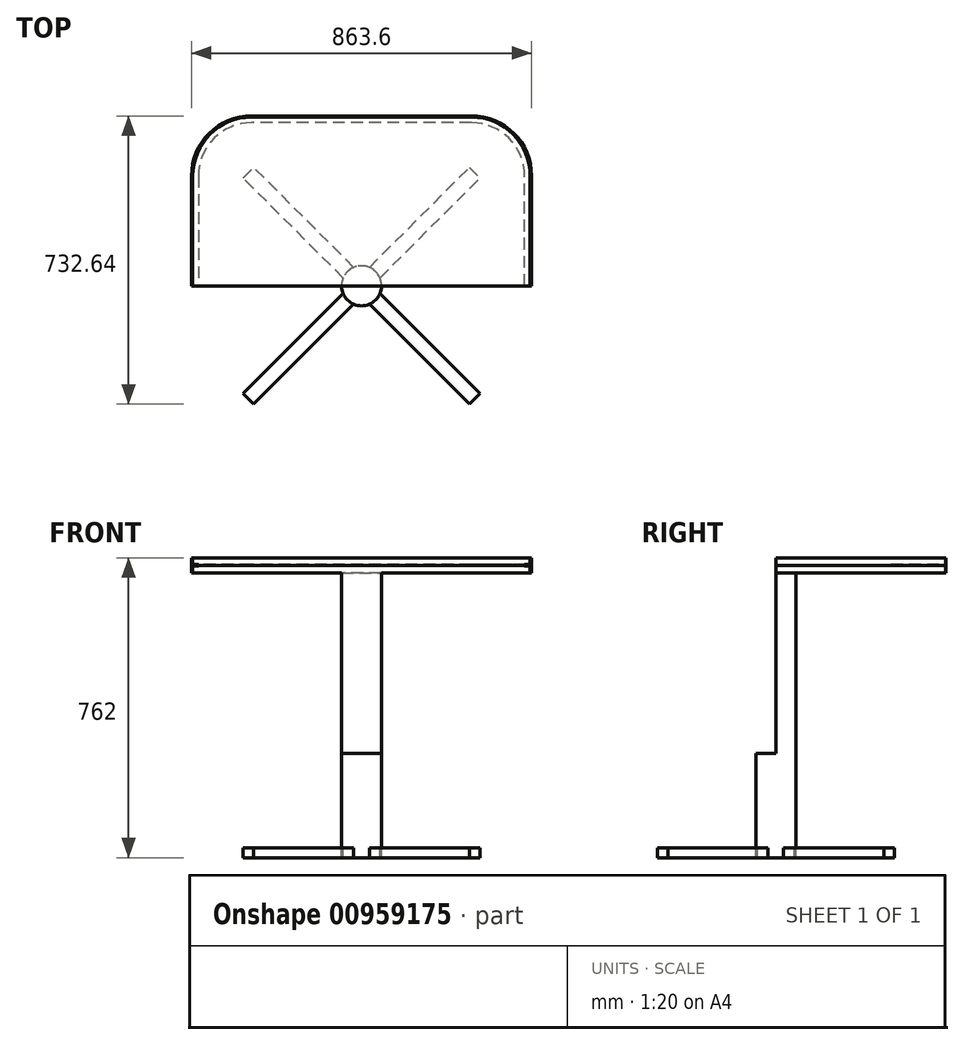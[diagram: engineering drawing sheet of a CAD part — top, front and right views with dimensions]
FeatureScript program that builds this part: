
annotation { "Feature Type Name" : "Feature", "Feature Type Description" : "" }
export const myFeature = defineFeature(function(context is Context, id is Id, definition is map)
    precondition{}
    {
        {
            var Q0;
            Q0=qCreatedBy(makeId("Top.planeOp"),FACE);
            var sketch = newSketch(context, id + "F0", { "sketchPlane" : qUnion([Q0])});
            skLineSegment(sketch, "E0.bottom", {"start": v(-279.4, 431.8) * mm, "end": v(279.4, 431.8) * mm});
            skLineSegment(sketch, "E0.top", {"start": v(-279.4, -431.8) * mm, "end": v(279.4, -431.8) * mm});
            skLineSegment(sketch, "E0.left", {"start": v(-431.8, 279.4) * mm, "end": v(-431.8, -279.4) * mm});
            skLineSegment(sketch, "E0.right", {"start": v(431.8, 279.4) * mm, "end": v(431.8, -279.4) * mm});
            skPoint(sketch, "E0.middle", {"position": v(0, 0) * mm});
            skPoint(sketch, "E1.visualSharp", {"position": v(-431.8, 431.8) * mm});
            skArc(sketch, "E1.filletArc", {"start": v(-279.4, 431.8) * mm, "mid": v(-387.16, 387.16) * mm, "end": v(-431.8, 279.4) * mm});
            skPoint(sketch, "E2.visualSharp", {"position": v(431.8, 431.8) * mm});
            skArc(sketch, "E2.filletArc", {"start": v(431.8, 279.4) * mm, "mid": v(387.16, 387.16) * mm, "end": v(279.4, 431.8) * mm});
            skPoint(sketch, "E3.visualSharp", {"position": v(431.8, -431.8) * mm});
            skArc(sketch, "E3.filletArc", {"start": v(279.4, -431.8) * mm, "mid": v(387.16, -387.16) * mm, "end": v(431.8, -279.4) * mm});
            skPoint(sketch, "E4.visualSharp", {"position": v(-431.8, -431.8) * mm});
            skArc(sketch, "E4.filletArc", {"start": v(-431.8, -279.4) * mm, "mid": v(-387.16, -387.16) * mm, "end": v(-279.4, -431.8) * mm});
            skSolve(sketch);
        }
        {
            var Q0;
            Q0=qSketchRegion(id+"F0",true);
            extrude(context, id + "F1", {"entities" : qUnion([Q0]), "oppositeDirection" : true, "depth" : 19.05 * mm, "offsetDistance" : 25.4 * mm});
        }
        {
            var Q0;
            Q0=makeQuery(id+"F1.opExtrude","CAP_FACE",FACE,{"disambiguationData":[OSD([sQuery(id+"F0.wireOp",EDGE,"E0.bottom"),sQuery(id+"F0.wireOp",EDGE,"E0.top"),sQuery(id+"F0.wireOp",EDGE,"E0.left"),sQuery(id+"F0.wireOp",EDGE,"E0.right"),sQuery(id+"F0.wireOp",EDGE,"E1.filletArc"),sQuery(id+"F0.wireOp",EDGE,"E2.filletArc"),sQuery(id+"F0.wireOp",EDGE,"E3.filletArc"),sQuery(id+"F0.wireOp",EDGE,"E4.filletArc")])],"isStart":false});
            var sketch = newSketch(context, id + "F2", { "sketchPlane" : qUnion([Q0])});
            skArc(sketch, "E5.0", {"start": v(-431.8, 279.4) * mm, "mid": v(-387.16, 387.16) * mm, "end": v(-279.4, 431.8) * mm});
            skLineSegment(sketch, "E6.0", {"start": v(-279.4, 431.8) * mm, "end": v(279.4, 431.8) * mm});
            skArc(sketch, "E7.0", {"start": v(279.4, 431.8) * mm, "mid": v(387.16, 387.16) * mm, "end": v(431.8, 279.4) * mm});
            skLineSegment(sketch, "E8.0", {"start": v(431.8, -279.4) * mm, "end": v(431.8, 279.4) * mm});
            skArc(sketch, "E9.0", {"start": v(431.8, -279.4) * mm, "mid": v(387.16, -387.16) * mm, "end": v(279.4, -431.8) * mm});
            skLineSegment(sketch, "E10.0", {"start": v(-279.4, -431.8) * mm, "end": v(279.4, -431.8) * mm});
            skArc(sketch, "E11.0", {"start": v(-279.4, -431.8) * mm, "mid": v(-387.16, -387.16) * mm, "end": v(-431.8, -279.4) * mm});
            skLineSegment(sketch, "E12.0", {"start": v(-431.8, -279.4) * mm, "end": v(-431.8, 279.4) * mm});
            skSolve(sketch);
        }
        {
            var Q0;
            Q0=makeQuery(id+"F2.imprint","IMPRINT",FACE,{"disambiguationData":[TD([[makeQuery(id+"F2.imprint","IMPRINT",EDGE,{"derivedFrom":sQuery(id+"F2.wireOp",EDGE,"E5.0")}),-1.0]])]});
            extrude(context, id + "F3", {"entities" : qUnion([Q0]), "depth" : 19.05 * mm, "offsetDistance" : 25.4 * mm});
        }
        {
            var Q0;
            Q0=qCreatedBy(makeId("Front.planeOp"),FACE);
            var sketch = newSketch(context, id + "F4", { "sketchPlane" : qUnion([Q0])});
            skLineSegment(sketch, "E13.0", {"start": v(-428.63, 0) * mm, "end": v(-431.8, 0) * mm});
            skLineSegment(sketch, "E14.0", {"start": v(-431.8, -19.05) * mm, "end": v(-431.8, 0) * mm});
            skLineSegment(sketch, "E15.0", {"start": v(-431.8, -38.1) * mm, "end": v(-431.8, -19.05) * mm});
            skLineSegment(sketch, "E16.0", {"start": v(-431.8, -38.1) * mm, "end": v(-428.63, -38.1) * mm});
            skLineSegment(sketch, "E17.bottom", {"start": v(-414.4, -17.46) * mm, "end": v(-428.63, -17.46) * mm});
            skLineSegment(sketch, "E17.top", {"start": v(-414.4, -20.64) * mm, "end": v(-428.63, -20.64) * mm});
            skLineSegment(sketch, "E17.left", {"start": v(-414.4, -17.46) * mm, "end": v(-414.4, -20.64) * mm});
            skPoint(sketch, "E17.middle", {"position": v(-431.8, -19.05) * mm});
            skLineSegment(sketch, "E18.bottom", {"start": v(-431.8, 0) * mm, "end": v(-428.63, 0) * mm});
            skLineSegment(sketch, "E18.left", {"start": v(-431.8, 0) * mm, "end": v(-431.8, -38.1) * mm});
            skLineSegment(sketch, "E18.right", {"start": v(-428.63, 0) * mm, "end": v(-428.63, -38.1) * mm});
            skPoint(sketch, "E17.right.start.orphan", {"position": v(-449.2, -17.46) * mm});
            skPoint(sketch, "E19.orphan", {"position": v(-449.2, -20.64) * mm});
            skPoint(sketch, "E20.orphan", {"position": v(-279.4, 0) * mm});
            skPoint(sketch, "E21.0.end.orphan", {"position": v(-279.4, -19.05) * mm});
            skPoint(sketch, "E22.orphan", {"position": v(-279.4, -38.1) * mm});
            skSolve(sketch);
        }
        {
            var Q0;
            Q0=qSketchRegion(id+"F4",true);
            var Q1;
            Q1=makeQuery(id+"F1.opExtrude","CAP_EDGE",EDGE,{"disambiguationData":[OSD([sQuery(id+"F0.wireOp",EDGE,"E0.top")])],"isStart":false});
            var Q2;
            Q2=makeQuery(id+"F1.opExtrude","CAP_EDGE",EDGE,{"disambiguationData":[OSD([sQuery(id+"F0.wireOp",EDGE,"E3.filletArc")])],"isStart":false});
            var Q3;
            Q3=makeQuery(id+"F1.opExtrude","CAP_EDGE",EDGE,{"disambiguationData":[OSD([sQuery(id+"F0.wireOp",EDGE,"E0.right")])],"isStart":false});
            var Q4;
            Q4=makeQuery(id+"F1.opExtrude","CAP_EDGE",EDGE,{"disambiguationData":[OSD([sQuery(id+"F0.wireOp",EDGE,"E4.filletArc")])],"isStart":false});
            var Q5;
            Q5=makeQuery(id+"F1.opExtrude","CAP_EDGE",EDGE,{"disambiguationData":[OSD([sQuery(id+"F0.wireOp",EDGE,"E1.filletArc")])],"isStart":false});
            var Q6;
            Q6=makeQuery(id+"F1.opExtrude","CAP_EDGE",EDGE,{"disambiguationData":[OSD([sQuery(id+"F0.wireOp",EDGE,"E0.left")])],"isStart":false});
            var Q7;
            Q7=makeQuery(id+"F1.opExtrude","CAP_EDGE",EDGE,{"disambiguationData":[OSD([sQuery(id+"F0.wireOp",EDGE,"E0.bottom")])],"isStart":false});
            var Q8;
            Q8=makeQuery(id+"F1.opExtrude","CAP_EDGE",EDGE,{"disambiguationData":[OSD([sQuery(id+"F0.wireOp",EDGE,"E2.filletArc")])],"isStart":false});
            sweep(context, id + "F5", {"profiles" : qUnion([Q0]), "path" : qUnion([Q1, Q2, Q3, Q4, Q5, Q6, Q7, Q8])});
        }
        {
            var Q0;
            Q0=makeQuery(id+"F3.opExtrude","CAP_FACE",FACE,{"disambiguationData":[OSD([sQuery(id+"F2.wireOp",EDGE,"E5.0"),sQuery(id+"F2.wireOp",EDGE,"E6.0"),sQuery(id+"F2.wireOp",EDGE,"E7.0"),sQuery(id+"F2.wireOp",EDGE,"E8.0"),sQuery(id+"F2.wireOp",EDGE,"E9.0"),sQuery(id+"F2.wireOp",EDGE,"E10.0"),sQuery(id+"F2.wireOp",EDGE,"E11.0"),sQuery(id+"F2.wireOp",EDGE,"E12.0")])],"isStart":false});
            var sketch = newSketch(context, id + "F6", { "sketchPlane" : qUnion([Q0])});
            skCircle(sketch, "E23", {"center": v(0, 0) * mm, "radius": 50.8 * mm});
            skSolve(sketch);
        }
        {
            var Q0;
            Q0=qSketchRegion(id+"F6",true);
            extrude(context, id + "F7", {"entities" : qUnion([Q0]), "operationType" : NewBodyOperationType.ADD, "depth" : 723.9 * mm, "offsetDistance" : 25.4 * mm});
        }
        {
            var Q0;
            Q0=makeQuery(id+"F7.opExtrude","CAP_FACE",FACE,{"disambiguationData":[OSD([sQuery(id+"F6.wireOp",EDGE,"E23")])],"isStart":false});
            var sketch = newSketch(context, id + "F8", { "sketchPlane" : qUnion([Q0])});
            skLineSegment(sketch, "E24", {"start": v(0, 0) * mm, "end": v(0, 334.88) * mm, "construction": true});
            skLineSegment(sketch, "E25.0", {"start": v(13.47, 13.47) * mm, "end": v(-273.9, 300.84) * mm});
            skLineSegment(sketch, "E26.0", {"start": v(-13.47, -13.47) * mm, "end": v(-300.84, 273.9) * mm});
            skLineSegment(sketch, "E27", {"start": v(-273.9, 300.84) * mm, "end": v(-300.84, 273.9) * mm});
            skLineSegment(sketch, "E28", {"start": v(13.47, 13.47) * mm, "end": v(-13.47, -13.47) * mm});
            skLineSegment(sketch, "E29.1.0", {"start": v(-13.47, 13.47) * mm, "end": v(-300.84, -273.9) * mm});
            skLineSegment(sketch, "E29.1.1", {"start": v(-300.84, -273.9) * mm, "end": v(-273.9, -300.84) * mm});
            skLineSegment(sketch, "E29.1.2", {"start": v(13.47, -13.47) * mm, "end": v(-273.9, -300.84) * mm});
            skLineSegment(sketch, "E29.1.3", {"start": v(-13.47, 13.47) * mm, "end": v(13.47, -13.47) * mm});
            skLineSegment(sketch, "E29.2.0", {"start": v(-13.47, -13.47) * mm, "end": v(273.9, -300.84) * mm});
            skLineSegment(sketch, "E29.2.1", {"start": v(273.9, -300.84) * mm, "end": v(300.84, -273.9) * mm});
            skLineSegment(sketch, "E29.2.2", {"start": v(13.47, 13.47) * mm, "end": v(300.84, -273.9) * mm});
            skLineSegment(sketch, "E29.2.3", {"start": v(-13.47, -13.47) * mm, "end": v(13.47, 13.47) * mm});
            skLineSegment(sketch, "E29.3.0", {"start": v(13.47, -13.47) * mm, "end": v(300.84, 273.9) * mm});
            skLineSegment(sketch, "E29.3.1", {"start": v(300.84, 273.9) * mm, "end": v(273.9, 300.84) * mm});
            skLineSegment(sketch, "E29.3.2", {"start": v(-13.47, 13.47) * mm, "end": v(273.9, 300.84) * mm});
            skLineSegment(sketch, "E29.3.3", {"start": v(13.47, -13.47) * mm, "end": v(-13.47, 13.47) * mm});
            skPoint(sketch, "E29.center", {"position": v(0, 0) * mm});
            skSolve(sketch);
        }
        {
            var Q0;
            Q0=qSketchRegion(id+"F8",true);
            extrude(context, id + "F9", {"entities" : qUnion([Q0]), "operationType" : NewBodyOperationType.ADD, "oppositeDirection" : true, "depth" : 25.4 * mm, "offsetDistance" : 25.4 * mm});
        }
        {
            var Q0;
            Q0=qCreatedBy(makeId("Front.planeOp"),FACE);
            var sketch = newSketch(context, id + "F10", { "sketchPlane" : qUnion([Q0])});
            skLineSegment(sketch, "E30.bottom", {"start": v(633.67, 496.97) * mm, "end": v(-633.67, 496.97) * mm});
            skLineSegment(sketch, "E30.top", {"start": v(633.67, -496.97) * mm, "end": v(-633.67, -496.97) * mm});
            skLineSegment(sketch, "E30.left", {"start": v(633.67, 496.97) * mm, "end": v(633.67, -496.97) * mm});
            skLineSegment(sketch, "E30.right", {"start": v(-633.67, 496.97) * mm, "end": v(-633.67, -496.97) * mm});
            skPoint(sketch, "E30.middle", {"position": v(0, 0) * mm});
            skSolve(sketch);
        }
        {
            var Q0;
            Q0 = qSketchRegion(id + "F10", true);
            extrude(context, id + "F11", {"entities" : qUnion([Q0]), "operationType" : NewBodyOperationType.REMOVE, "depth" : 914.4 * mm, "offsetDistance" : 25.4 * mm});
        }
    });
